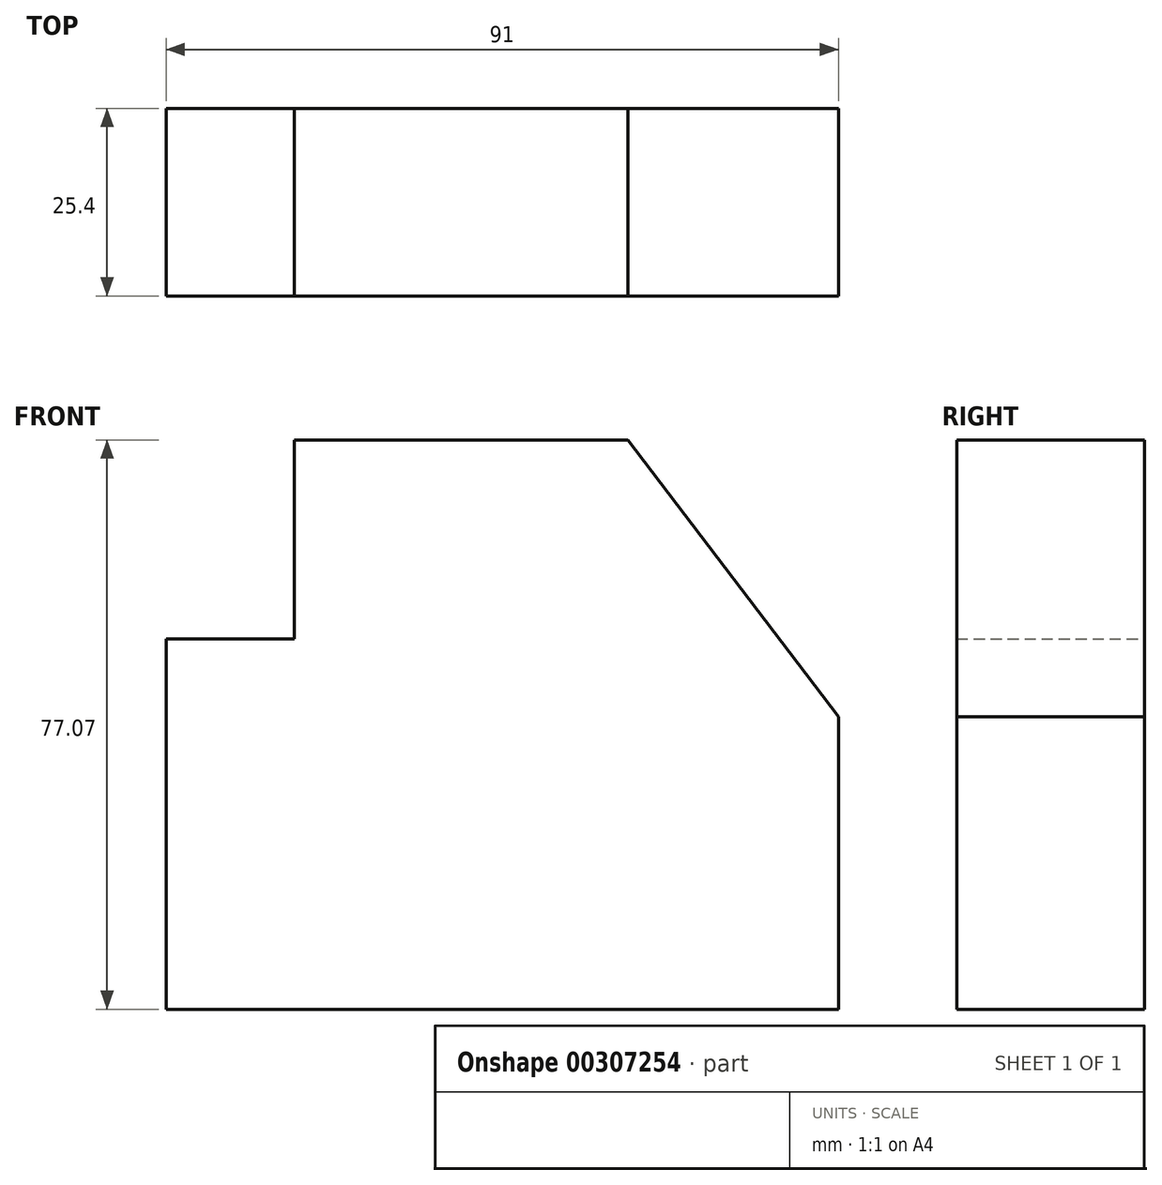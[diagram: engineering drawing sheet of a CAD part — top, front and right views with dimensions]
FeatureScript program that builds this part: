
annotation { "Feature Type Name" : "Feature", "Feature Type Description" : "" }
export const myFeature = defineFeature(function(context is Context, id is Id, definition is map)
    precondition{}
    {
        {
            var Q0;
            Q0=qCreatedBy(makeId("Front.planeOp"),FACE);
            var sketch = newSketch(context, id + "F0", { "sketchPlane" : qUnion([Q0])});
            skLineSegment(sketch, "E0", {"start": v(50.14, -5.73) * mm, "end": v(50.14, -45.34) * mm});
            skLineSegment(sketch, "E1", {"start": v(50.14, -45.34) * mm, "end": v(-40.86, -45.34) * mm});
            skLineSegment(sketch, "E2", {"start": v(-40.86, -45.34) * mm, "end": v(-40.86, 4.8) * mm});
            skLineSegment(sketch, "E3", {"start": v(-40.86, 4.8) * mm, "end": v(-23.52, 4.8) * mm});
            skLineSegment(sketch, "E4", {"start": v(-23.52, 4.8) * mm, "end": v(-23.52, 31.73) * mm});
            skLineSegment(sketch, "E5", {"start": v(-23.52, 31.73) * mm, "end": v(21.67, 31.73) * mm});
            skLineSegment(sketch, "E6", {"start": v(21.67, 31.73) * mm, "end": v(50.14, -5.73) * mm});
            skSolve(sketch);
        }
        {
            var Q0;
            Q0=makeQuery(id+"F0.imprint","IMPRINT",FACE,{"disambiguationData":[TD([[makeQuery(id+"F0.imprint","IMPRINT",EDGE,{"derivedFrom":sQuery(id+"F0.wireOp",EDGE,"E0")}),-1.0]])]});
            extrude(context, id + "F1", {"entities" : qUnion([Q0]), "depth" : 25.4 * mm});
        }
    });
